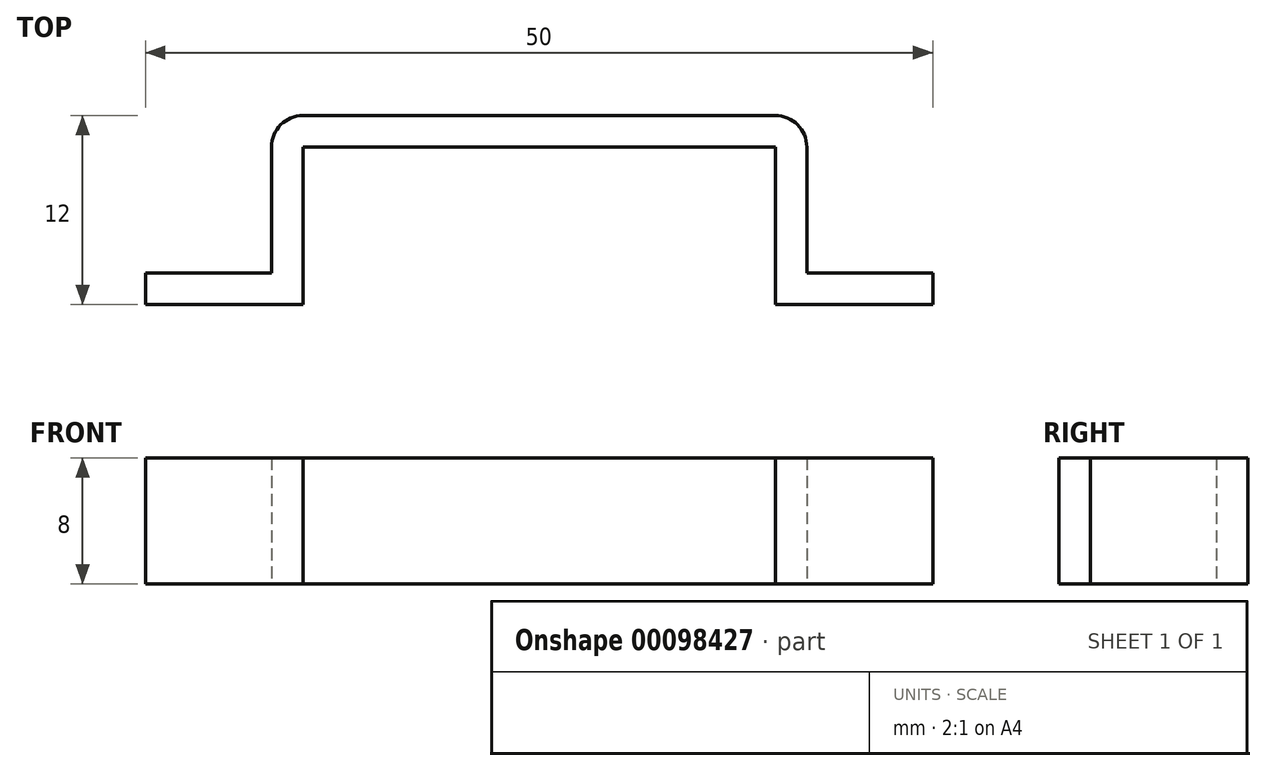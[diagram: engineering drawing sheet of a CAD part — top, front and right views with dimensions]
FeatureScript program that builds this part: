
annotation { "Feature Type Name" : "Feature", "Feature Type Description" : "" }
export const myFeature = defineFeature(function(context is Context, id is Id, definition is map)
    precondition{}
    {
        {
            var Q0;
            Q0=qCreatedBy(makeId("Top.planeOp"),FACE);
            var sketch = newSketch(context, id + "F0", { "sketchPlane" : qUnion([Q0])});
            skLineSegment(sketch, "E0", {"start": v(0, 0) * mm, "end": v(10, 0) * mm});
            skLineSegment(sketch, "E1", {"start": v(10, 0) * mm, "end": v(10, 10) * mm});
            skLineSegment(sketch, "E2", {"start": v(10, 10) * mm, "end": v(40, 10) * mm});
            skLineSegment(sketch, "E3", {"start": v(40, 10) * mm, "end": v(40, 0) * mm});
            skLineSegment(sketch, "E4", {"start": v(40, 0) * mm, "end": v(50, 0) * mm});
            skLineSegment(sketch, "E5", {"start": v(0, 0) * mm, "end": v(0, 2) * mm});
            skLineSegment(sketch, "E6", {"start": v(0, 2) * mm, "end": v(8, 2) * mm});
            skLineSegment(sketch, "E7", {"start": v(8, 2) * mm, "end": v(8, 12) * mm});
            skLineSegment(sketch, "E8", {"start": v(8, 12) * mm, "end": v(42, 12) * mm});
            skLineSegment(sketch, "E9", {"start": v(42, 12) * mm, "end": v(42, 2) * mm});
            skLineSegment(sketch, "E10", {"start": v(42, 2) * mm, "end": v(50, 2) * mm});
            skLineSegment(sketch, "E11", {"start": v(50, 2) * mm, "end": v(50, 0) * mm});
            skSolve(sketch);
        }
        {
            var Q0;
            Q0 = qSketchRegion(id + "F0", true);
            extrude(context, id + "F1", {"entities" : qUnion([Q0]), "depth" : 8 * mm});
        }
        {
            var Q0;
            Q0=makeQuery(id+"F1.opExtrude","SWEPT_EDGE",EDGE,{"disambiguationData":[OSD([sQuery(id+"F0.wireOp",EDGE,"E7"),sQuery(id+"F0.wireOp",EDGE,"E8")])]});
            var Q1;
            Q1=makeQuery(id+"F1.opExtrude","SWEPT_EDGE",EDGE,{"disambiguationData":[OSD([sQuery(id+"F0.wireOp",EDGE,"E8"),sQuery(id+"F0.wireOp",EDGE,"E9")])]});
            fillet(context, id + "F2", {"entities" : qUnion([Q0, Q1]), "radius" : 2 * mm, "tangentPropagation" : true, "allowEdgeOverflow" : false});
        }
    });
